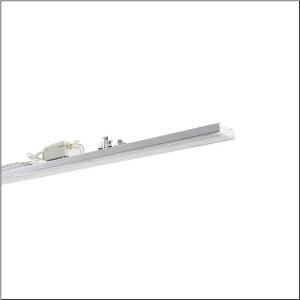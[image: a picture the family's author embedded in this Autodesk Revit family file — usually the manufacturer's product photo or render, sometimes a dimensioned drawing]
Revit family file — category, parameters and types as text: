
# Revit family: licross_r__21_recessed_ho_52tl1emn4e5s_ecfe
name_source: partatom
category: Lighting Fixtures
units: mm (PartAtom-declared; Revit-internal decimal feet)

## family parameters
Cut with Voids When Loaded = No
Host = Face
Light Source = No
Part Type = Normal
Room Calculation Point = No
Round Connector Dimension = Use Diameter
Shared = No

## types (1)
- --- (1 x LED, 14710 lm, 83.1 W, 4000K)
    Apparent Load = 83 VA
    CIE Flux Codes = 85 95 99 100 100
    Color Rendering = 80
    Color Temperature = 4000K
    Default Elevation = 1800 mm
    Description = Licross® 21 Recessed HO, luminaire insert, of sheet steel, galvanised, coil coated, white, length: 1.500mm, width: 66mm, height: 67mm, LED rated luminous flux: 14.710lm, light colour: 840, control gear: ON/OFF Multilumen, with plug, 3-pole, with phase selection, mains connection: 220..240V, AC, 50/60Hz, rated input power: 83W, halogen-free wiring, primary light control with lens, of plastic, primary optical cover: cover, of PMMA, light emission: direct distribution, primary light characteristic: symmetric, protection rating (complete): IP40, insulation class (complete): insulation class I (protective earthing), certification: CE, ENEC, VDE, UKCA, protection symbol: D if used in an environment without relevant dust loads with corresponding accessories, impact resistance: IK06, permissible ambient temperature for indoor applications: -35..+30°C, corresponds to IFS (International Featured Standards) requirements for safety and quality in the food industry, reducing of maximum allowable ambient temperature of 5°C with ceiling mounting, LABS conformity tested according to VDMA 24364:2018-05, packaging unit: 1 piece
    Height = 58 mm
    Lamp = 1 x LED
    Lamp Light Flux = 14710 lm
    Lamp Power = 83.1 W
    Lamp count = 1
    Length = 1500 mm
    Luminous efficacy = 177 lm/W
    Manufacturer = Siteco
    ModVariant = No
    Model = 52TL1EMN4E5S
    Mounting Place = Ceiling
    Mounting Type = Pendant
    Number of Poles = 1
    OnlyDefault = Yes
    Power Factor = 1
    Product Name = Licross® 21 Recessed HO
    Product group = luminaire insert
    ProductGroupID = 901
    Protection Class = Protection class I
    Protection Degree = IP 40
    RLX_Detail_Level = 1
    RLX_Emergency_Light_Flux = 0 lm
    RLX_Emergency_Type = 0
    RLX_Emergency_Type_DB = No
    RlxData = <blob elided: 22373 chars, md5=83817baa>
    Socket = socket
    Standby Power = 0 W
    System Light Flux = 14710 lm
    System Power = 83 W
    Type Comments = factory setting: luminous flux: 100 % | (A | C | E) | 195 mA
    Type Image = l_1296930.jpg
    URL = http://relux.com
    VarID = @adj_036621
    Voltage = 0 V
    Weight = 0.00 kg
    Width = 66 mm

## geometry (parser evidence)
native form markers: Blend x4, Sweep x9
no freeform markers — native parametric forms only
